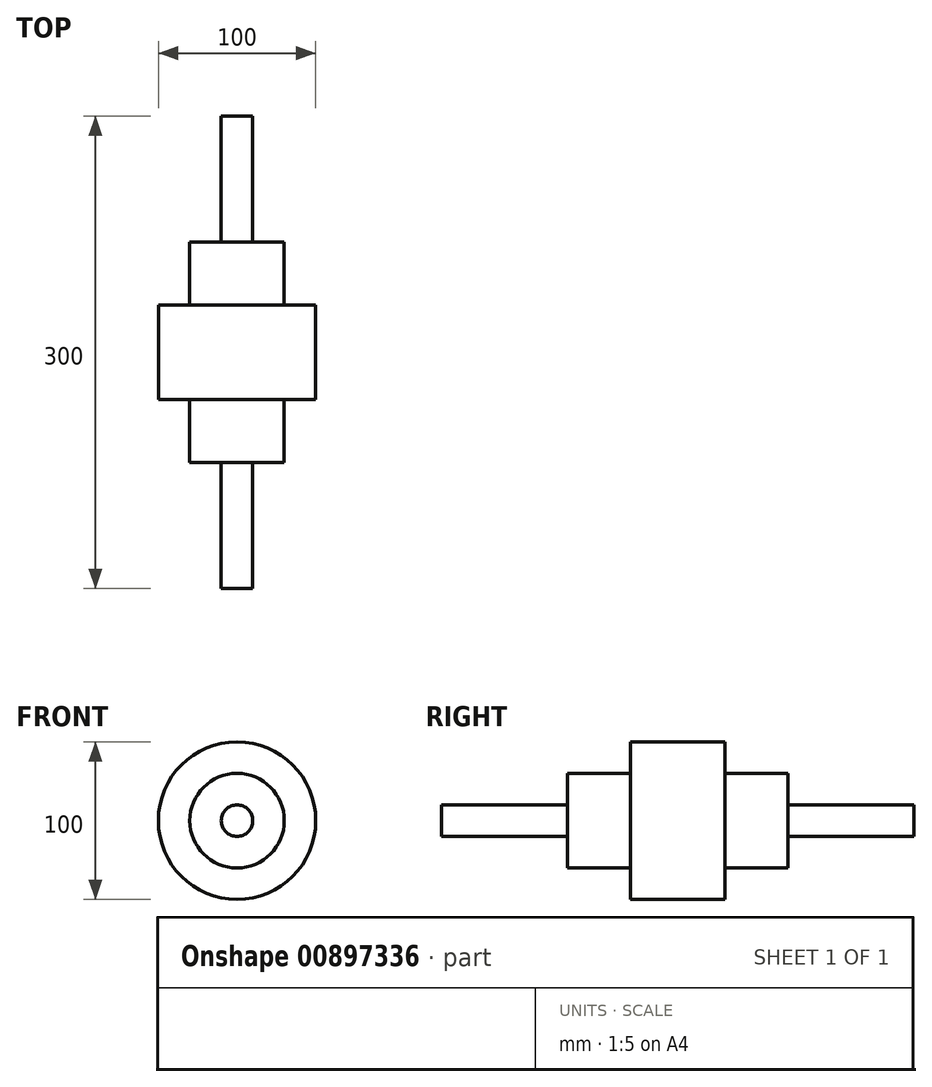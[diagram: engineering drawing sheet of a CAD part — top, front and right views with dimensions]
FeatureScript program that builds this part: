
annotation { "Feature Type Name" : "Feature", "Feature Type Description" : "" }
export const myFeature = defineFeature(function(context is Context, id is Id, definition is map)
    precondition{}
    {
        {
            var Q0;
            Q0=qCreatedBy(makeId("Front.planeOp"),FACE);
            var sketch = newSketch(context, id + "F0", { "sketchPlane" : qUnion([Q0])});
            skCircle(sketch, "E0", {"center": v(0, 0) * mm, "radius": 50 * mm});
            skSolve(sketch);
        }
        {
            var Q0;
            Q0 = qSketchRegion(id + "F0", true);
            extrude(context, id + "F1", {"entities" : qUnion([Q0]), "depth" : 60 * mm, "offsetDistance" : 25.4 * mm});
        }
        {
            var Q0;
            Q0=makeQuery(id+"F1.opExtrude","CAP_FACE",FACE,{"disambiguationData":[OSD([sQuery(id+"F0.wireOp",EDGE,"E0")])],"isStart":true});
            var sketch = newSketch(context, id + "F2", { "sketchPlane" : qUnion([Q0])});
            skCircle(sketch, "E1", {"center": v(0, 0) * mm, "radius": 30 * mm});
            skSolve(sketch);
        }
        {
            var Q0;
            Q0 = qSketchRegion(id + "F2", true);
            extrude(context, id + "F3", {"entities" : qUnion([Q0]), "operationType" : NewBodyOperationType.ADD, "depth" : 40 * mm, "offsetDistance" : 25.4 * mm});
        }
        {
            var Q0;
            Q0=makeQuery(id+"F1.opExtrude","CAP_FACE",FACE,{"disambiguationData":[OSD([sQuery(id+"F0.wireOp",EDGE,"E0")])],"isStart":false});
            var sketch = newSketch(context, id + "F4", { "sketchPlane" : qUnion([Q0])});
            skCircle(sketch, "E2", {"center": v(0, 0) * mm, "radius": 30 * mm});
            skSolve(sketch);
        }
        {
            var Q0;
            Q0 = qSketchRegion(id + "F4", true);
            extrude(context, id + "F5", {"entities" : qUnion([Q0]), "operationType" : NewBodyOperationType.ADD, "depth" : 40 * mm, "offsetDistance" : 25.4 * mm});
        }
        {
            var Q0;
            Q0=makeQuery(id+"F3.opExtrude","CAP_FACE",FACE,{"disambiguationData":[OSD([sQuery(id+"F2.wireOp",EDGE,"E1")])],"isStart":false});
            var sketch = newSketch(context, id + "F6", { "sketchPlane" : qUnion([Q0])});
            skCircle(sketch, "E3", {"center": v(0, 0) * mm, "radius": 10 * mm});
            skSolve(sketch);
        }
        {
            var Q0;
            Q0 = qSketchRegion(id + "F6", true);
            extrude(context, id + "F7", {"entities" : qUnion([Q0]), "operationType" : NewBodyOperationType.ADD, "depth" : 80 * mm, "offsetDistance" : 25.4 * mm});
        }
        {
            var Q0;
            Q0=makeQuery(id+"F5.opExtrude","CAP_FACE",FACE,{"disambiguationData":[OSD([sQuery(id+"F4.wireOp",EDGE,"E2")])],"isStart":false});
            var sketch = newSketch(context, id + "F8", { "sketchPlane" : qUnion([Q0])});
            skCircle(sketch, "E4", {"center": v(0, 0) * mm, "radius": 10 * mm});
            skSolve(sketch);
        }
        {
            var Q0;
            Q0=makeQuery(id+"F8.imprint","IMPRINT",FACE,{"disambiguationData":[TD([[makeQuery(id+"F8.imprint","IMPRINT",EDGE,{"derivedFrom":sQuery(id+"F8.wireOp",EDGE,"E4")}),1.0]])]});
            extrude(context, id + "F9", {"entities" : qUnion([Q0]), "operationType" : NewBodyOperationType.ADD, "depth" : 80 * mm, "offsetDistance" : 25.4 * mm});
        }
    });
